FCSTD DOCUMENT  (FreeCAD 0.18R16146 (Git))
Label: virtual_wall_fc
License: All rights reserved
LicenseURL: http://en.wikipedia.org/wiki/All_rights_reserved
objects: Sketcher::SketchObject×1, PartDesign::Body×1
note: 2 computed .brp shape members not serialized (recipe doc carries the construction recipe); baked Part::Feature solids carry a one-line shape summary decoded from their .brp

FEATURE [Sketcher::SketchObject] Sketch
  MapMode = 5
  Support = -> [XY_Plane]
  sketch-geometry (20):
    g0: LineSegment StartX=0 StartY=0 StartZ=0 EndX=110 EndY=0 EndZ=0
    g1: LineSegment StartX=110 StartY=0 StartZ=0 EndX=110 EndY=80 EndZ=0
    g2: LineSegment StartX=110 StartY=80 StartZ=0 EndX=0 EndY=80 EndZ=0
    g3: LineSegment StartX=0 StartY=80 StartZ=0 EndX=0 EndY=0 EndZ=0
    g4: LineSegment StartX=2 StartY=10 StartZ=0 EndX=2 EndY=70 EndZ=0
    g5: LineSegment StartX=2 StartY=70 StartZ=0 EndX=10 EndY=70 EndZ=0
    g6: LineSegment StartX=10 StartY=70 StartZ=0 EndX=10 EndY=78 EndZ=0
    g7: LineSegment StartX=10 StartY=78 StartZ=0 EndX=100 EndY=78 EndZ=0
    g8: LineSegment StartX=100 StartY=78 StartZ=0 EndX=100 EndY=70 EndZ=0
    g9: LineSegment StartX=100 StartY=70 StartZ=0 EndX=108 EndY=70 EndZ=0
    g10: LineSegment StartX=108 StartY=70 StartZ=0 EndX=108 EndY=10 EndZ=0
    g11: LineSegment StartX=108 StartY=10 StartZ=0 EndX=100 EndY=10 EndZ=0
    g12: LineSegment StartX=100 StartY=10 StartZ=0 EndX=100 EndY=2 EndZ=0
    g13: LineSegment StartX=100 StartY=2 StartZ=0 EndX=10 EndY=2 EndZ=0
    g14: LineSegment StartX=10 StartY=2 StartZ=0 EndX=10 EndY=10 EndZ=0
    g15: LineSegment StartX=10 StartY=10 StartZ=0 EndX=2 EndY=10 EndZ=0
    g16: Circle CenterX=6 CenterY=74 CenterZ=0 NormalX=0 NormalY=0 NormalZ=1 AngleXU=0 Radius=1.9
    g17: Circle CenterX=104 CenterY=74 CenterZ=0 NormalX=0 NormalY=0 NormalZ=1 AngleXU=0 Radius=1.9
    g18: Circle CenterX=104 CenterY=6 CenterZ=0 NormalX=0 NormalY=0 NormalZ=1 AngleXU=0 Radius=1.9
    g19: Circle CenterX=6 CenterY=6 CenterZ=0 NormalX=0 NormalY=0 NormalZ=1 AngleXU=0 Radius=1.9
  constraints (59):
    c: Coincident(g0,g1)
    c: Coincident(g1,g2)
    c: Coincident(g2,g3)
    c: Coincident(g3,g0)
    c: Horizontal(g0)
    c: Vertical(g1)
    c: Coincident(g0,g-1)
    c: DistanceX(g2,g2) = 110
    c: DistanceY(g3,g3) = 80
    c: Vertical(g4)
    c: Coincident(g4,g5)
    c: Horizontal(g5)
    c: Coincident(g5,g6)
    c: Vertical(g6)
    c: Coincident(g6,g7)
    c: Horizontal(g7)
    c: Coincident(g7,g8)
    c: Vertical(g8)
    c: Coincident(g8,g9)
    c: Horizontal(g9)
    c: Coincident(g9,g10)
    c: Vertical(g10)
    c: Coincident(g10,g11)
    c: Horizontal(g11)
    c: Coincident(g11,g12)
    c: Vertical(g12)
    c: Coincident(g12,g13)
    c: Horizontal(g13)
    c: Coincident(g13,g14)
    c: Vertical(g14)
    c: Coincident(g15,g14)
    c: Coincident(g15,g4)
    c: Horizontal(g15)
    c: DistanceX(g4) = 2
    c: DistanceY(g13) = 2
    c: DistanceX(g4,g5) = 8
    c: DistanceY(g5,g6) = 8
    c: DistanceX(g10,g0) = 2
    c: DistanceX(g11,g10) = 8
    c: DistanceY(g12,g11) = 8
    c: DistanceX(g8,g9) = 8
    c: DistanceY(g8,g7) = 8
    c: DistanceX(g4,g14) = 8
    c: DistanceY(g13,g14) = 8
    c: Equal(g0,g2)
    c: Equal(g3,g1)
    c: DistanceY(g6,g2) = 2
    c: DistanceX(g2,g16) = 6
    c: DistanceY(g16,g2) = 6
    c: Radius(g16) = 1.9
    c: DistanceX(g17,g1) = 6
    c: DistanceY(g17,g1) = 6
    c: Radius(g17) = 1.9
    c: DistanceY(g0,g18) = 6
    c: DistanceX(g18,g0) = 6
    c: Radius(g18) = 1.9
    c: Radius(g19) = 1.9
    c: DistanceX(g0,g19) = 6
    c: DistanceY(g0,g19) = 6
FEATURE [PartDesign::Body] Body
  Group = -> [Sketch]
  Origin = -> Origin
